# Revit family: QF_MACOM_FF72C
name_source: partatom
category: Equipamento especial
units: mm (PartAtom-declared; Revit-internal decimal feet)

## family parameters
Com base no plano de trabalho = Não
Compartilhado = Não
Corte com vazios quando carregada = Não
Cota do conector redondo = Utilizar diâmetro
Número OmniClass = 23.40.40.14.17.11
Ponto de cálculo do ambiente = Não
Sempre na vertical = Sim
Tipo de parte = Normal
Título OmniClass = Cookers, Ovens, Stoves

## types (2) — shared parameters
Descrição = FOGÃO DE ENCOSTO COM FORNO MACOM
Electric Connection Height = 247,00 mm
Electrical Supply = 220 V
Elevação padrão = 0,00 mm
Fabricante = MACOM
Gas Connection Height (COOKER) = 329,00 mm
Gas Connection Height (OVEN) = 724,00 mm
Gas Pressure = 0,0 bar
Gas Size (COOKER) = 1"
Gas Size (OVEN) = 1"
Height = 900,00 mm
Length = 745,00 mm
Line Frequency = 60 Hz
Oven Capacity = 85,0 L
Show Clearances = Sim
Show Logo = Sim
URL = http://www.acosmacom.com.br
Volume = 0,49 m³
Weight = 100,00 kg
Width = 720,00 mm

## per-type parameters (varying)
| type | Gas Consumption GLP (COOKER) | Gas Consumption GLP (OVEN) | Gas Consumption GN (COOKER) | Gas Consumption GN (OVEN) | Gas Input GLP (COOKER) | Gas Input GLP (OVEN) | Gas Input GN (COOKER) | Gas Input GN (OVEN) |
| FF72C-N |  |  | 1,82 m³/h | 0,51 m³/h | 0 Btu/h | 0 Btu/h | 17222 Kcal/h | 4896 Kcal/h |
| FF72C-G | 1,5 Kg/h | 0,43 Kg/h | 0,00 m³/h | 0,00 m³/h | 68388 Btu/h | 19427 Btu/h |  |  |

note: column(s) folded — value = type name in every type: Modelo

## geometry (parser evidence)
native form markers: Sweep x10
no freeform markers — native parametric forms only
